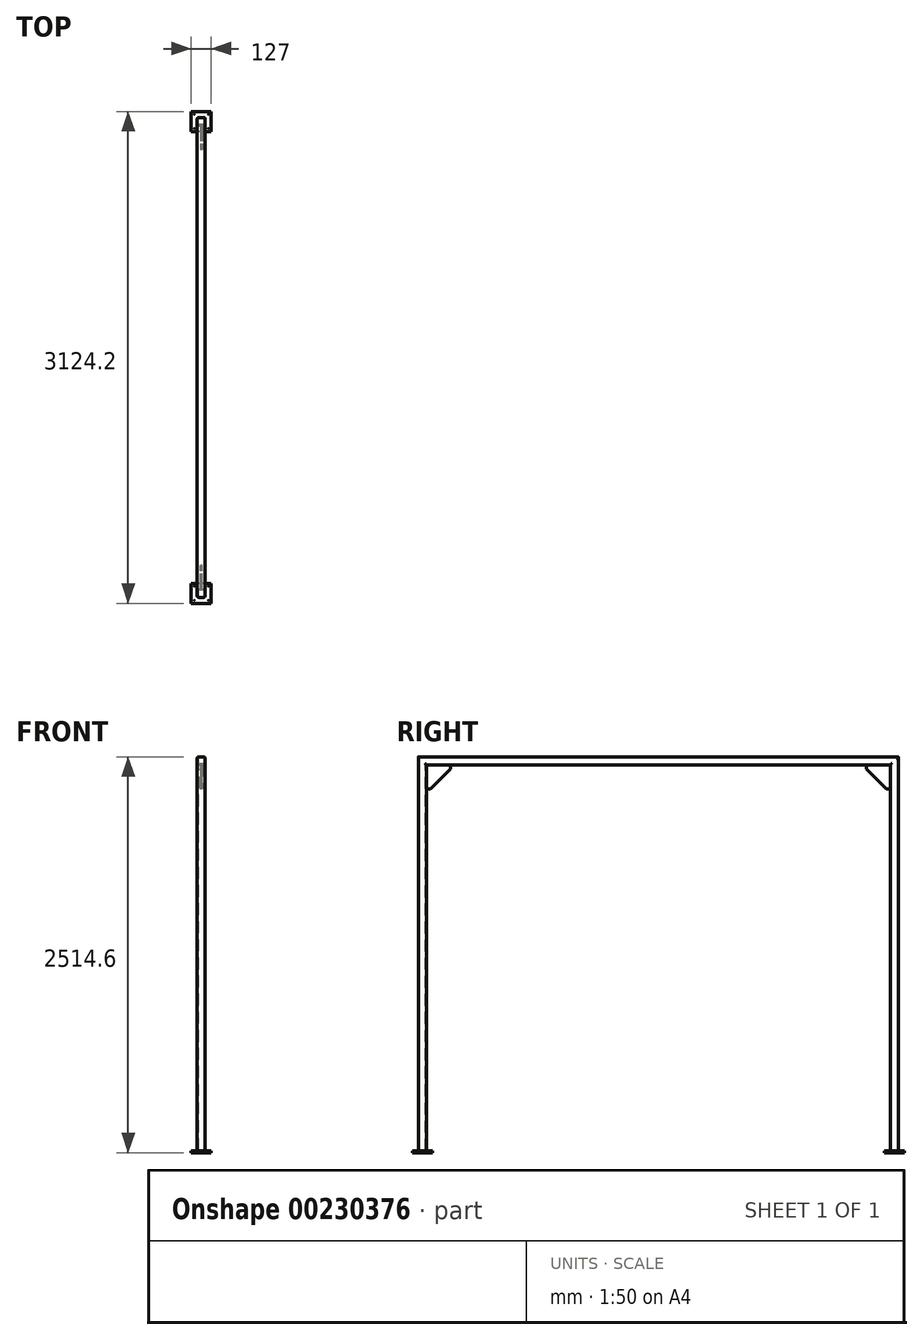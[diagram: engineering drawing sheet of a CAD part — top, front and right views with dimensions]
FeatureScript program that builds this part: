
annotation { "Feature Type Name" : "Feature", "Feature Type Description" : "" }
export const myFeature = defineFeature(function(context is Context, id is Id, definition is map)
    precondition{}
    {
        {
            var Q0;
            Q0=qCreatedBy(makeId("Right.planeOp"),FACE);
            var sketch = newSketch(context, id + "F0", { "sketchPlane" : qUnion([Q0])});
            skLineSegment(sketch, "E0.top", {"start": v(-1524, 2501.9) * mm, "end": v(1524, 2501.9) * mm});
            skLineSegment(sketch, "E0.left", {"start": v(-1524, 0) * mm, "end": v(-1524, 2501.9) * mm});
            skLineSegment(sketch, "E0.right", {"start": v(1524, 0) * mm, "end": v(1524, 2501.9) * mm});
            skSolve(sketch);
        }
        {
            var Q0;
            Q0=qCreatedBy(makeId("Top.planeOp"),FACE);
            var sketch = newSketch(context, id + "F1", { "sketchPlane" : qUnion([Q0])});
            skPoint(sketch, "E1.0", {"position": v(0, -1524) * mm});
            skLineSegment(sketch, "E2", {"start": v(0, -1524) * mm, "end": v(15.75, -1524) * mm});
            skLineSegment(sketch, "E3", {"start": v(25.4, -1514.35) * mm, "end": v(25.4, -1482.85) * mm});
            skLineSegment(sketch, "E4", {"start": v(15.75, -1473.2) * mm, "end": v(-15.75, -1473.2) * mm});
            skLineSegment(sketch, "E5", {"start": v(-25.4, -1482.85) * mm, "end": v(-25.4, -1514.35) * mm});
            skLineSegment(sketch, "E6", {"start": v(-15.75, -1524) * mm, "end": v(0, -1524) * mm});
            skPoint(sketch, "E7.visualSharp", {"position": v(25.4, -1524) * mm});
            skArc(sketch, "E7.filletArc", {"start": v(15.75, -1524) * mm, "mid": v(22.57, -1521.17) * mm, "end": v(25.4, -1514.35) * mm});
            skPoint(sketch, "E8.visualSharp", {"position": v(25.4, -1473.2) * mm});
            skArc(sketch, "E8.filletArc", {"start": v(25.4, -1482.85) * mm, "mid": v(22.57, -1476.03) * mm, "end": v(15.75, -1473.2) * mm});
            skPoint(sketch, "E9.visualSharp", {"position": v(-25.4, -1473.2) * mm});
            skArc(sketch, "E9.filletArc", {"start": v(-15.75, -1473.2) * mm, "mid": v(-22.57, -1476.03) * mm, "end": v(-25.4, -1482.85) * mm});
            skPoint(sketch, "E10.visualSharp", {"position": v(-25.4, -1524) * mm});
            skArc(sketch, "E10.filletArc", {"start": v(-25.4, -1514.35) * mm, "mid": v(-22.57, -1521.17) * mm, "end": v(-15.75, -1524) * mm});
            skLineSegment(sketch, "E11.0", {"start": v(-15.75, -1519.24) * mm, "end": v(0, -1519.24) * mm});
            skArc(sketch, "E11.1", {"start": v(-20.64, -1514.35) * mm, "mid": v(-19.2, -1517.8) * mm, "end": v(-15.75, -1519.24) * mm});
            skLineSegment(sketch, "E11.2", {"start": v(-20.64, -1482.85) * mm, "end": v(-20.64, -1514.35) * mm});
            skArc(sketch, "E11.3", {"start": v(-15.75, -1477.96) * mm, "mid": v(-19.2, -1479.4) * mm, "end": v(-20.64, -1482.85) * mm});
            skArc(sketch, "E11.4", {"start": v(15.75, -1519.24) * mm, "mid": v(19.2, -1517.8) * mm, "end": v(20.64, -1514.35) * mm});
            skLineSegment(sketch, "E11.5", {"start": v(20.64, -1514.35) * mm, "end": v(20.64, -1482.85) * mm});
            skArc(sketch, "E11.6", {"start": v(20.64, -1482.85) * mm, "mid": v(19.2, -1479.4) * mm, "end": v(15.75, -1477.96) * mm});
            skLineSegment(sketch, "E11.7", {"start": v(15.75, -1477.96) * mm, "end": v(-15.75, -1477.96) * mm});
            skLineSegment(sketch, "E12.0", {"start": v(0, -1519.24) * mm, "end": v(15.75, -1519.24) * mm});
            skSolve(sketch);
        }
        {
            var Q0;
            Q0=makeQuery(id+"F1.imprint","IMPRINT",FACE,{"disambiguationData":[TD([[makeQuery(id+"F1.imprint","IMPRINT",EDGE,{"derivedFrom":sQuery(id+"F1.wireOp",EDGE,"E2")}),1.0]])]});
            var Q1;
            Q1=sQuery(id+"F0.wireOp",EDGE,"E0.left");
            var Q2;
            Q2=sQuery(id+"F0.wireOp",EDGE,"E0.top");
            var Q3;
            Q3=sQuery(id+"F0.wireOp",EDGE,"E0.right");
            sweep(context, id + "F2", {"profiles" : qUnion([Q0]), "path" : qUnion([Q1, Q2, Q3])});
        }
        {
            var Q0;
            Q0=makeQuery(id+"F2.opSweep","CAP_FACE",FACE,{"disambiguationData":[OSD([sQuery(id+"F0.wireOp",VERTEX,"E0.left.start"),sQuery(id+"F1.wireOp",EDGE,"E2"),sQuery(id+"F1.wireOp",EDGE,"E3"),sQuery(id+"F1.wireOp",EDGE,"E4"),sQuery(id+"F1.wireOp",EDGE,"E5"),sQuery(id+"F1.wireOp",EDGE,"E6"),sQuery(id+"F1.wireOp",EDGE,"E7.filletArc"),sQuery(id+"F1.wireOp",EDGE,"E8.filletArc"),sQuery(id+"F1.wireOp",EDGE,"E9.filletArc"),sQuery(id+"F1.wireOp",EDGE,"E10.filletArc"),sQuery(id+"F1.wireOp",EDGE,"E11.0"),sQuery(id+"F1.wireOp",EDGE,"E11.1"),sQuery(id+"F1.wireOp",EDGE,"E11.2"),sQuery(id+"F1.wireOp",EDGE,"E11.3"),sQuery(id+"F1.wireOp",EDGE,"E11.4"),sQuery(id+"F1.wireOp",EDGE,"E11.5"),sQuery(id+"F1.wireOp",EDGE,"E11.6"),sQuery(id+"F1.wireOp",EDGE,"E11.7"),sQuery(id+"F1.wireOp",EDGE,"E12.0")])],"isStart":true});
            var sketch = newSketch(context, id + "F3", { "sketchPlane" : qUnion([Q0])});
            skLineSegment(sketch, "E13.0", {"start": v(-15.75, 1524) * mm, "end": v(15.75, 1524) * mm, "construction": true});
            skLineSegment(sketch, "E14.0", {"start": v(15.75, 1473.2) * mm, "end": v(-15.75, 1473.2) * mm, "construction": true});
            skLineSegment(sketch, "E15", {"start": v(0, 1524) * mm, "end": v(0, 1473.2) * mm, "construction": true});
            skLineSegment(sketch, "E16.bottom", {"start": v(63.5, 1562.1) * mm, "end": v(-63.5, 1562.1) * mm});
            skLineSegment(sketch, "E16.top", {"start": v(63.5, 1435.1) * mm, "end": v(-63.5, 1435.1) * mm});
            skLineSegment(sketch, "E16.left", {"start": v(63.5, 1562.1) * mm, "end": v(63.5, 1435.1) * mm});
            skLineSegment(sketch, "E16.right", {"start": v(-63.5, 1562.1) * mm, "end": v(-63.5, 1435.1) * mm});
            skPoint(sketch, "E16.middle", {"position": v(0, 1498.6) * mm});
            skLineSegment(sketch, "E17.left", {"start": v(-63.5, 1435.1) * mm, "end": v(-63.5, 1562.1) * mm});
            skLineSegment(sketch, "E18.0", {"start": v(-15.75, -1473.2) * mm, "end": v(15.75, -1473.2) * mm, "construction": true});
            skLineSegment(sketch, "E19.0", {"start": v(-15.75, -1524) * mm, "end": v(15.75, -1524) * mm, "construction": true});
            skLineSegment(sketch, "E20", {"start": v(0, -1473.2) * mm, "end": v(0, -1524) * mm, "construction": true});
            skLineSegment(sketch, "E21", {"start": v(0, -1501.83) * mm, "end": v(-72.48, -1501.83) * mm, "construction": true});
            skPoint(sketch, "E17.top.end.orphan", {"position": v(-241.3, 1562.1) * mm});
            skSolve(sketch);
        }
        {
            var Q0;
            Q0=qSketchRegion(id+"F3",true);
            extrude(context, id + "F4", {"entities" : qUnion([Q0]), "depth" : 12.7 * mm});
        }
        {
            var Q0;
            Q0=makeQuery(id+"F4.opExtrude","CAP_FACE",FACE,{"disambiguationData":[OSD([sQuery(id+"F3.wireOp",EDGE,"E16.bottom"),sQuery(id+"F3.wireOp",EDGE,"E16.top"),sQuery(id+"F3.wireOp",EDGE,"E16.left"),sQuery(id+"F3.wireOp",EDGE,"E17.bottom"),sQuery(id+"F3.wireOp",EDGE,"E17.top"),sQuery(id+"F3.wireOp",EDGE,"E17.right")])],"isStart":false});
            var sketch = newSketch(context, id + "F5", { "sketchPlane" : qUnion([Q0])});
            skLineSegment(sketch, "E22.0", {"start": v(-44.45, 1435.1) * mm, "end": v(-44.45, 1562.1) * mm, "construction": true});
            skLineSegment(sketch, "E23.0", {"start": v(63.5, 1543.05) * mm, "end": v(-266.7, 1543.05) * mm, "construction": true});
            skLineSegment(sketch, "E24.0", {"start": v(44.45, 1562.1) * mm, "end": v(44.45, 1435.1) * mm, "construction": true});
            skLineSegment(sketch, "E25.0", {"start": v(63.5, 1454.15) * mm, "end": v(-266.7, 1454.15) * mm, "construction": true});
            skPoint(sketch, "E26", {"position": v(-44.45, 1454.15) * mm});
            skPoint(sketch, "E27", {"position": v(-44.45, 1543.05) * mm});
            skPoint(sketch, "E28", {"position": v(44.45, 1543.05) * mm});
            skPoint(sketch, "E29", {"position": v(44.45, 1454.15) * mm});
            skSolve(sketch);
        }
        {
            var Q0;
            Q0=sQuery(id+"F5.wireOp",VERTEX,"E26");
            var Q1;
            Q1=sQuery(id+"F5.wireOp",VERTEX,"E27");
            var Q2;
            Q2=sQuery(id+"F5.wireOp",VERTEX,"E28");
            var Q3;
            Q3=sQuery(id+"F5.wireOp",VERTEX,"E29");
            var Q4;
            Q4=makeQuery(id+"F4.opExtrude","SWEPT_BODY",BODY,{"disambiguationData":[OSD([sQuery(id+"F3.wireOp",EDGE,"E16.bottom"),sQuery(id+"F3.wireOp",EDGE,"E16.top"),sQuery(id+"F3.wireOp",EDGE,"E16.left"),sQuery(id+"F3.wireOp",EDGE,"E17.bottom"),sQuery(id+"F3.wireOp",EDGE,"E17.top"),sQuery(id+"F3.wireOp",EDGE,"E17.right")])]});
            hole(context, id + "F6", {"style" : HoleStyle.SIMPLE, "endStyle" : HoleEndStyle.THROUGH, "standardTappedOrClearance" : lookupTablePath({ "standard" : "ANSI", "size" : "9/16 (0.56)", "type" : "Drilled" }), "standardBlindInLast" : lookupTablePath({ "standard" : "ANSI", "size" : "9/16", "type" : "Drilled" }), "holeDiameter" : 9 / 406.4 * mm, "startFromSketch" : true, "locations" : qUnion([Q0, Q1, Q2, Q3]), "scope" : qUnion([Q4]), "isTappedThrough" : true});
        }
        {
            var Q0;
            Q0=makeQuery(id+"F4.opExtrude","SWEPT_BODY",BODY,{"disambiguationData":[OSD([sQuery(id+"F3.wireOp",EDGE,"E16.bottom"),sQuery(id+"F3.wireOp",EDGE,"E16.top"),sQuery(id+"F3.wireOp",EDGE,"E16.left"),sQuery(id+"F3.wireOp",EDGE,"E17.bottom"),sQuery(id+"F3.wireOp",EDGE,"E17.top"),sQuery(id+"F3.wireOp",EDGE,"E17.right")])]});
            var Q1;
            Q1=makeQuery(id+"F8T19zNGPlvkzio_2.opExtrude","SWEPT_BODY",BODY,{"disambiguationData":[OSD([sQuery(id+"FdzXDW9Q1HgexBr_2.wireOp",EDGE,"4KvRzeDM-CwYW-YYCa-esWh-QIO9w4eAwdw9.bottom"),sQuery(id+"FdzXDW9Q1HgexBr_2.wireOp",EDGE,"4KvRzeDM-CwYW-YYCa-esWh-QIO9w4eAwdw9.top"),sQuery(id+"FdzXDW9Q1HgexBr_2.wireOp",EDGE,"4KvRzeDM-CwYW-YYCa-esWh-QIO9w4eAwdw9.left"),sQuery(id+"FdzXDW9Q1HgexBr_2.wireOp",EDGE,"4KvRzeDM-CwYW-YYCa-esWh-QIO9w4eAwdw9.right"),sQuery(id+"FdzXDW9Q1HgexBr_2.wireOp",EDGE,"qLC7WOi8-mBCz-45bP-6HAC-S5qomJN4AdET")])]});
            var Q2;
            Q2=qCreatedBy(makeId("Front.planeOp"),FACE);
            mirror(context, id + "F7", {"entities" : qUnion([Q0, Q1]), "mirrorPlane" : qUnion([Q2])});
        }
        {
            var Q0;
            Q0=makeQuery(id+"F2.opSweep","SWEPT_FACE",FACE,{"disambiguationData":[OSD([sQuery(id+"F0.wireOp",EDGE,"E0.left"),sQuery(id+"F1.wireOp",EDGE,"E3")])]});
            var Q1;
            Q1=makeQuery(id+"F2.opSweep","SWEPT_FACE",FACE,{"disambiguationData":[OSD([sQuery(id+"F0.wireOp",EDGE,"E0.left"),sQuery(id+"F1.wireOp",EDGE,"E5")])]});
            cPlane(context, id + "F8", {"entities" : qUnion([Q0, Q1]), "cplaneType" : CPlaneType.MID_PLANE, "offset" : 25.4 * mm, "width" : 152.4 * mm, "height" : 152.4 * mm});
        }
        {
            var Q0;
            Q0=qCreatedBy(id+"F8.planeOp",FACE);
            var sketch = newSketch(context, id + "F9", { "sketchPlane" : qUnion([Q0])});
            skLineSegment(sketch, "E30.0", {"start": v(-1473.2, 2451.1) * mm, "end": v(1473.2, 2451.1) * mm, "construction": true});
            skLineSegment(sketch, "E31.0", {"start": v(-1473.2, 0) * mm, "end": v(-1473.2, 2451.1) * mm, "construction": true});
            skLineSegment(sketch, "E32.bottom", {"start": v(-1473.2, 2451.1) * mm, "end": v(-1320.8, 2451.1) * mm});
            skLineSegment(sketch, "E32.top", {"start": v(-1473.2, 2298.7) * mm, "end": v(-1447.8, 2298.7) * mm});
            skLineSegment(sketch, "E32.left", {"start": v(-1473.2, 2451.1) * mm, "end": v(-1473.2, 2298.7) * mm});
            skLineSegment(sketch, "E32.right", {"start": v(-1320.8, 2451.1) * mm, "end": v(-1320.8, 2425.7) * mm});
            skLineSegment(sketch, "E33.0", {"start": v(-1473.2, 2425.7) * mm, "end": v(1473.2, 2425.7) * mm, "construction": true});
            skLineSegment(sketch, "E34.0", {"start": v(-1447.8, 0) * mm, "end": v(-1447.8, 2451.1) * mm, "construction": true});
            skLineSegment(sketch, "E35", {"start": v(-1447.8, 2298.7) * mm, "end": v(-1320.8, 2425.7) * mm});
            skSolve(sketch);
        }
        {
            var Q0;
            Q0=qSketchRegion(id+"F9",true);
            extrude(context, id + "F10", {"entities" : qUnion([Q0]), "endBound" : BoundingType.SYMMETRIC, "depth" : 9.52 * mm});
        }
        {
            var Q0;
            Q0=makeQuery(id+"F10.opExtrude","SWEPT_BODY",BODY,{"disambiguationData":[OSD([sQuery(id+"F9.wireOp",EDGE,"E32.bottom"),sQuery(id+"F9.wireOp",EDGE,"E32.top"),sQuery(id+"F9.wireOp",EDGE,"E32.left"),sQuery(id+"F9.wireOp",EDGE,"E32.right"),sQuery(id+"F9.wireOp",EDGE,"E35")])]});
            var Q1;
            Q1=qCreatedBy(makeId("Front.planeOp"),FACE);
            mirror(context, id + "F11", {"operationType" : NewBodyOperationType.ADD, "entities" : qUnion([Q0]), "mirrorPlane" : qUnion([Q1])});
        }
    });
